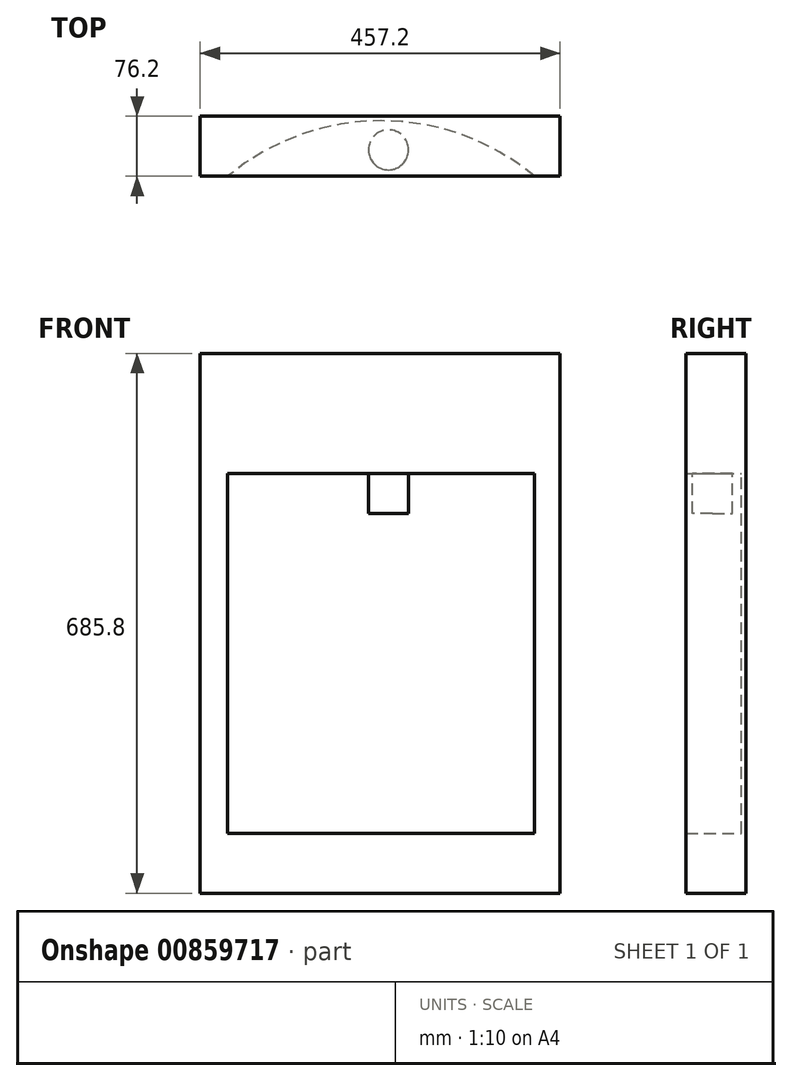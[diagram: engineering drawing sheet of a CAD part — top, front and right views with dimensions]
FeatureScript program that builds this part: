
annotation { "Feature Type Name" : "Feature", "Feature Type Description" : "" }
export const myFeature = defineFeature(function(context is Context, id is Id, definition is map)
    precondition{}
    {
        {
            var Q0;
            Q0=qCreatedBy(makeId("Front.planeOp"),FACE);
            var sketch = newSketch(context, id + "F0", { "sketchPlane" : qUnion([Q0])});
            skLineSegment(sketch, "E0.bottom", {"start": v(-191.8, 570.3) * mm, "end": v(265.4, 570.3) * mm});
            skLineSegment(sketch, "E0.top", {"start": v(-191.8, -115.5) * mm, "end": v(265.4, -115.5) * mm});
            skLineSegment(sketch, "E0.left", {"start": v(-191.8, 570.3) * mm, "end": v(-191.8, -115.5) * mm});
            skLineSegment(sketch, "E0.right", {"start": v(265.4, 570.3) * mm, "end": v(265.4, -115.5) * mm});
            skSolve(sketch);
        }
        {
            var Q0;
            Q0=makeQuery(id+"F0.imprint","IMPRINT",FACE,{"disambiguationData":[TD([[makeQuery(id+"F0.imprint","IMPRINT",EDGE,{"derivedFrom":sQuery(id+"F0.wireOp",EDGE,"E0.bottom")}),-1.0]])]});
            extrude(context, id + "F1", {"entities" : qUnion([Q0]), "depth" : 76.2 * mm, "offsetDistance" : 25.4 * mm});
        }
        {
            var Q0;
            Q0=makeQuery(id+"F1.opExtrude","SWEPT_FACE",FACE,{"disambiguationData":[OSD([sQuery(id+"F0.wireOp",EDGE,"E0.bottom")])]});
            var sketch = newSketch(context, id + "F2", { "sketchPlane" : qUnion([Q0])});
            skCircle(sketch, "E1", {"center": v(38.08, -310.46) * mm, "radius": 304.8 * mm});
            skSolve(sketch);
        }
        {
            var Q0;
            {var subQ0=sQuery(id+"F2.wireOp",EDGE,"E1");var subQ1=makeQuery(id+"F1.opExtrude","CAP_EDGE",EDGE,{"disambiguationData":[OSD([sQuery(id+"F0.wireOp",EDGE,"E0.bottom")])],"isStart":false});var subQ2=makeQuery(id+"F2.imprint","INTERSECT",VERTEX,{"disambiguationData":[OD(0.0)],"derivedFrom":[subQ1,subQ0]});Q0=makeQuery(id+"F2.imprint","IMPRINT",FACE,{"disambiguationData":[TD([[makeQuery(id+"F2.imprint","IMPRINT",EDGE,{"disambiguationData":[TD([[subQ2,1.0]])],"derivedFrom":subQ0}),1.0]])]});}
            extrude(context, id + "F3", {"entities" : qUnion([Q0]), "operationType" : NewBodyOperationType.REMOVE, "oppositeDirection" : true, "depth" : 609.6 * mm, "offsetDistance" : 25.4 * mm, "hasSecondDirection" : true, "secondDirectionOppositeDirection" : true, "secondDirectionDepth" : 152.4 * mm});
        }
        {
            var Q0;
            Q0=makeQuery(id+"F3.boolean.opBoolean","COPY",FACE,{"derivedFrom":makeQuery(id+"F3.opExtrude","CAP_FACE",FACE,{"disambiguationData":[OSD([sQuery(id+"F0.wireOp",EDGE,"E0.bottom"),sQuery(id+"F2.wireOp",EDGE,"E1")])],"isStart":true})});
            var sketch = newSketch(context, id + "F4", { "sketchPlane" : qUnion([Q0])});
            skCircle(sketch, "E2", {"center": v(47.36, 42.68) * mm, "radius": 25.4 * mm});
            skSolve(sketch);
        }
        {
            var Q0;
            Q0=makeQuery(id+"F4.imprint","IMPRINT",FACE,{"disambiguationData":[TD([[makeQuery(id+"F4.imprint","IMPRINT",EDGE,{"derivedFrom":sQuery(id+"F4.wireOp",EDGE,"E2")}),1.0]])]});
            extrude(context, id + "F5", {"entities" : qUnion([Q0]), "operationType" : NewBodyOperationType.ADD, "depth" : 50.8 * mm, "offsetDistance" : 25.4 * mm});
        }
    });
